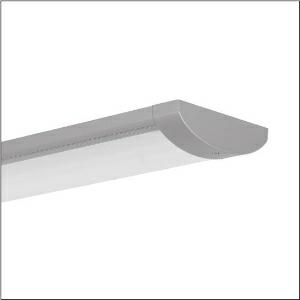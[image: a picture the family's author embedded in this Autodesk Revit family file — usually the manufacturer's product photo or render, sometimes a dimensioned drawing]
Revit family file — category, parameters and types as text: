
# Revit family: tv_20_5xa86174n0j
name_source: partatom
category: Lighting Fixtures
units: mm (PartAtom-declared; Revit-internal decimal feet)

## family parameters
Cut with Voids When Loaded = No
Host = Face
Light Source = No
Part Type = Normal
Room Calculation Point = No
Round Connector Dimension = Use Diameter
Shared = No

## types (1)
- TV 20 (1 x LED 4000K / CRI = 80 (unbekannt), 3960 lm, 4000K)
    Apparent Load = 37 VA
    CIE Flux Codes = 48 78 95 99 100
    Color Rendering = 80
    Color Temperature = 4000K
    Default Elevation = 1800 mm
    Description = TV 20, vandal-proof luminaire, primary light control with specular reflector, of aluminium, matt, primary optical cover: enclosure, of PC, frosted, light emission: direct distribution, primary light characteristic: symmetric, installation type: surface-mounted, LED, rated luminous flux: 3.960lm, luminous efficacy: 107lm/W, light colour: 840, colour temperature: 4000K, control gear: ON/OFF, mains connection: 230V, AC, 50Hz, rated input power: 37W, luminaire housing, of aluminium, coated, Siteco® metallic grey (DB 702S), with wall and ceiling fixing element, length: 1.261mm, width: 260mm, height: 70mm, mounting height: 2.5..4.0m, protection rating (complete): IP65, insulation class (complete): insulation class I (protective earthing), certification: CE, protection symbol: F, impact resistance: 2x IK10, standard: EN 60598, packaging unit: 1 piece
    Height = 70 mm
    Lamp = 1 x LED 4000K / CRI >= 80 (unbekannt)
    Lamp Light Flux = 3960 lm
    Lamp count = 1
    Length = 1261 mm
    Luminous efficacy = 107 lm/W
    Manufacturer = Siteco
    ModVariant = No
    Model = 5XA86174N0J
    Mounting Place = Ceiling
    Mounting Type = Surface mounted
    Number of Poles = 1
    OnlyDefault = Yes
    Power Factor = 1
    Product Name = TV 20
    Product group = vandal-proof luminaire
    ProductGroupID = 310
    Protection Class = Protection class I
    Protection Degree = IP 65
    RLX_Detail_Level = 1
    RLX_Emergency_Light_Flux = 0 lm
    RLX_Emergency_Type = 0
    RLX_Emergency_Type_DB = No
    RlxData = <blob elided: 25601 chars, md5=61e1c3ec>
    Socket = socket
    Standby Power = 0 W
    System Light Flux = 3960 lm
    System Power = 37 W
    Type Comments = Product without accessories
    Type Image = l_1004809.jpg
    URL = http://relux.com
    VarID = ---
    Voltage = 0 V
    Weight = 0.00 kg
    Width = 260 mm

## geometry (parser evidence)
native form markers: Blend x4, Sweep x12
no freeform markers — native parametric forms only
